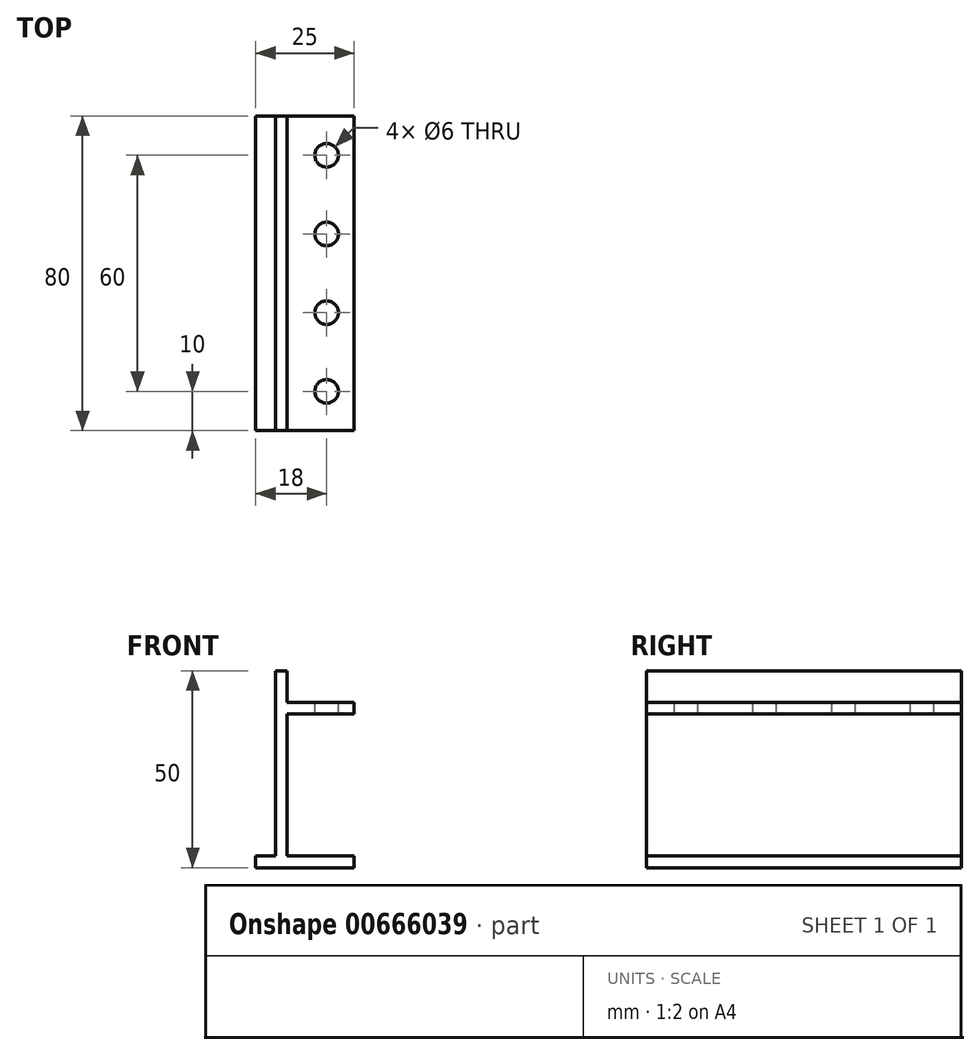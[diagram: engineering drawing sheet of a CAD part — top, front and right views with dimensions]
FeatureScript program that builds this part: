
annotation { "Feature Type Name" : "Feature", "Feature Type Description" : "" }
export const myFeature = defineFeature(function(context is Context, id is Id, definition is map)
    precondition{}
    {
        {
            var Q0;
            Q0=qCreatedBy(makeId("Top.planeOp"),FACE);
            var sketch = newSketch(context, id + "F0", { "sketchPlane" : qUnion([Q0])});
            skLineSegment(sketch, "E0.bottom", {"start": v(10, 40) * mm, "end": v(-10, 40) * mm});
            skLineSegment(sketch, "E0.top", {"start": v(10, -40) * mm, "end": v(-10, -40) * mm});
            skLineSegment(sketch, "E0.left", {"start": v(10, 40) * mm, "end": v(10, -40) * mm});
            skLineSegment(sketch, "E0.right", {"start": v(-10, 40) * mm, "end": v(-10, -40) * mm});
            skPoint(sketch, "E0.middle", {"position": v(0, 0) * mm});
            skSolve(sketch);
        }
        {
            var Q0;
            Q0 = qSketchRegion(id + "F0", true);
            extrude(context, id + "F1", {"entities" : qUnion([Q0]), "depth" : 50 * mm, "offsetDistance" : 25 * mm});
        }
        {
            var Q0;
            Q0=makeQuery(id+"F1.opExtrude","SWEPT_FACE",FACE,{"disambiguationData":[OSD([sQuery(id+"F0.wireOp",EDGE,"E0.top")])]});
            var sketch = newSketch(context, id + "F2", { "sketchPlane" : qUnion([Q0])});
            skLineSegment(sketch, "E1.bottom", {"start": v(10, 3) * mm, "end": v(-7, 3) * mm});
            skLineSegment(sketch, "E1.top", {"start": v(10, 39) * mm, "end": v(-7, 39) * mm});
            skLineSegment(sketch, "E1.left", {"start": v(10, 3) * mm, "end": v(10, 39) * mm});
            skLineSegment(sketch, "E1.right", {"start": v(-7, 3) * mm, "end": v(-7, 39) * mm});
            skLineSegment(sketch, "E2.bottom", {"start": v(10, 42) * mm, "end": v(-7, 42) * mm});
            skLineSegment(sketch, "E2.top", {"start": v(10, 50) * mm, "end": v(-7, 50) * mm});
            skLineSegment(sketch, "E2.left", {"start": v(10, 42) * mm, "end": v(10, 50) * mm});
            skLineSegment(sketch, "E2.right", {"start": v(-7, 42) * mm, "end": v(-7, 50) * mm});
            skSolve(sketch);
        }
        {
            var Q0;
            Q0 = qSketchRegion(id + "F2", true);
            extrude(context, id + "F3", {"entities" : qUnion([Q0]), "operationType" : NewBodyOperationType.REMOVE, "endBound" : BoundingType.THROUGH_ALL, "oppositeDirection" : true, "depth" : 25 * mm, "offsetDistance" : 25 * mm});
        }
        {
            var Q0;
            Q0=makeQuery(id+"F3.boolean.opBoolean","COPY",FACE,{"derivedFrom":makeQuery(id+"F3.opExtrude","SWEPT_FACE",FACE,{"disambiguationData":[OSD([sQuery(id+"F2.wireOp",EDGE,"E2.bottom")])]})});
            var sketch = newSketch(context, id + "F4", { "sketchPlane" : qUnion([Q0])});
            skCircle(sketch, "E3", {"center": v(3, -30) * mm, "radius": 3 * mm});
            skCircle(sketch, "E4", {"center": v(3, -10) * mm, "radius": 3 * mm});
            skCircle(sketch, "E5", {"center": v(3, 10) * mm, "radius": 3 * mm});
            skCircle(sketch, "E6", {"center": v(3, 30) * mm, "radius": 3 * mm});
            skSolve(sketch);
        }
        {
            var Q0;
            Q0 = qSketchRegion(id + "F4", true);
            extrude(context, id + "F5", {"entities" : qUnion([Q0]), "operationType" : NewBodyOperationType.REMOVE, "endBound" : BoundingType.UP_TO_NEXT, "oppositeDirection" : true, "depth" : 25 * mm, "offsetDistance" : 25 * mm});
        }
        {
            var Q0;
            Q0=makeQuery(id+"F1.opExtrude","SWEPT_FACE",FACE,{"disambiguationData":[OSD([sQuery(id+"F0.wireOp",EDGE,"E0.top")])]});
            var sketch = newSketch(context, id + "F6", { "sketchPlane" : qUnion([Q0])});
            skLineSegment(sketch, "E7.bottom", {"start": v(-10, 0) * mm, "end": v(-15, 0) * mm});
            skLineSegment(sketch, "E7.top", {"start": v(-10, 3) * mm, "end": v(-15, 3) * mm});
            skLineSegment(sketch, "E7.left", {"start": v(-10, 0) * mm, "end": v(-10, 3) * mm});
            skLineSegment(sketch, "E7.right", {"start": v(-15, 0) * mm, "end": v(-15, 3) * mm});
            skSolve(sketch);
        }
        {
            var Q0;
            Q0 = qSketchRegion(id + "F6", true);
            var Q1;
            Q1=makeQuery(id+"F1.opExtrude","SWEPT_FACE",FACE,{"disambiguationData":[OSD([sQuery(id+"F0.wireOp",EDGE,"E0.bottom")])]});
            extrude(context, id + "F7", {"entities" : qUnion([Q0]), "operationType" : NewBodyOperationType.ADD, "endBound" : BoundingType.UP_TO_SURFACE, "oppositeDirection" : true, "depth" : 25 * mm, "endBoundEntityFace" : qUnion([Q1]), "offsetDistance" : 25 * mm});
        }
    });
